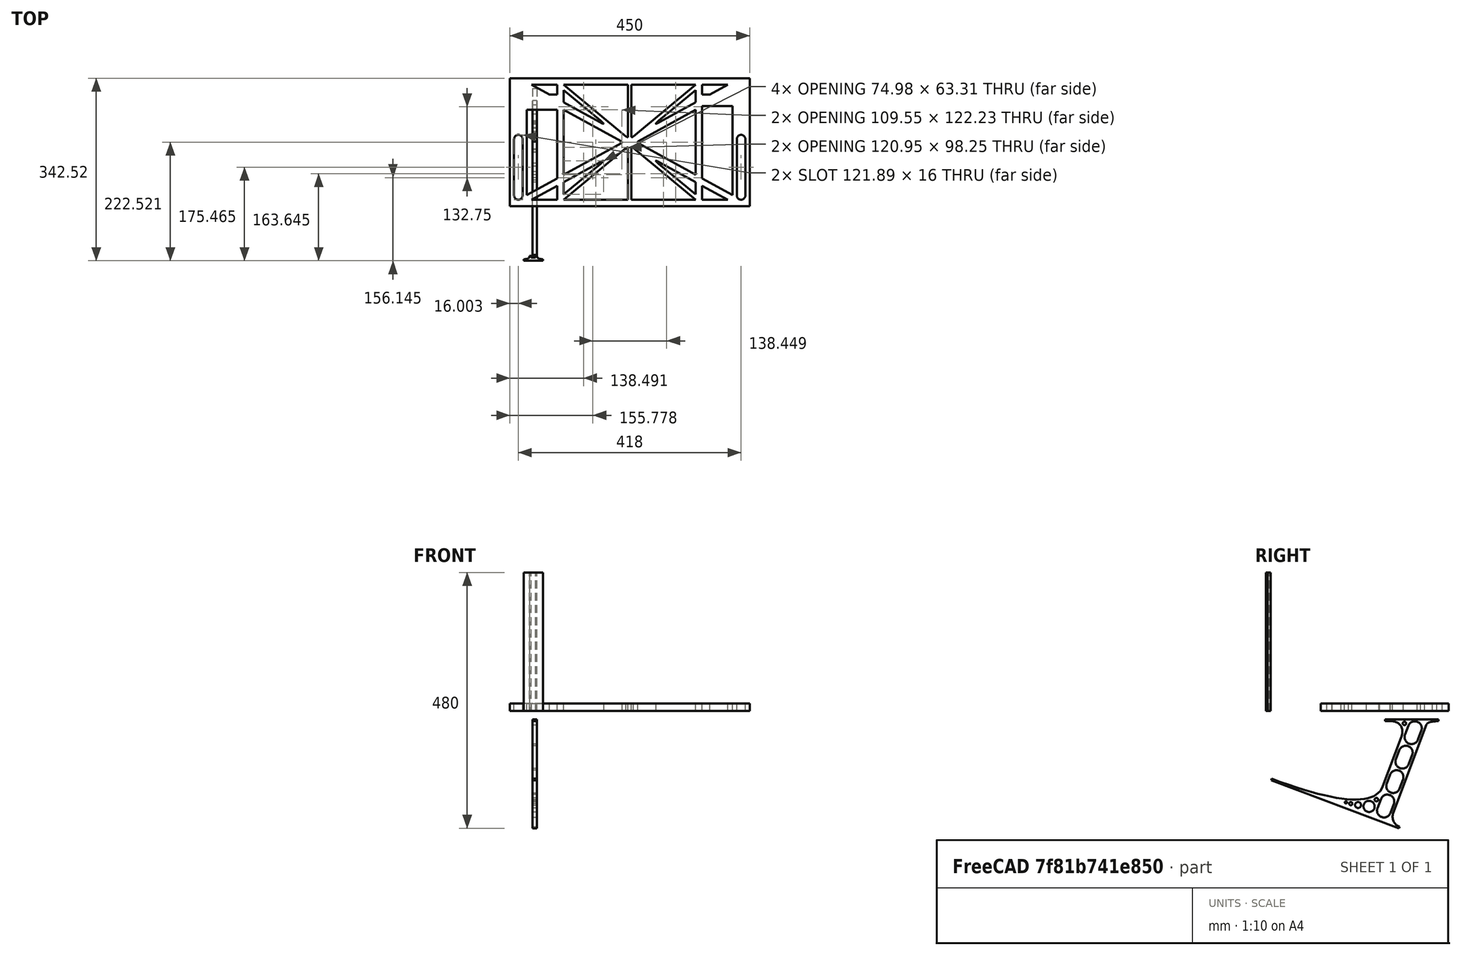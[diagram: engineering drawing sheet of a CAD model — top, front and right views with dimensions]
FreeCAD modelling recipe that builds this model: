
FCSTD DOCUMENT  (FreeCAD 0.19R0.19.2)
Label: laptopStand069
License: All rights reserved
LicenseURL: http://en.wikipedia.org/wiki/All_rights_reserved
objects: Sketcher::SketchObject×3, Part::Extrusion×3
note: 6 computed .brp shape members not serialized (recipe doc carries the construction recipe); baked Part::Feature solids carry a one-line shape summary decoded from their .brp

FEATURE [Sketcher::SketchObject] Sketch
  FullyConstrained = true
  sketch-geometry (124):
    g0: LineSegment StartX=-10.9272 StartY=-82.7794 StartZ=0 EndX=46.0728 EndY=-51.4823 EndZ=0
    g1: LineSegment StartX=366.073 StartY=-91.7794 StartZ=0 EndX=318.073 EndY=-65.424 EndZ=0
    g2: LineSegment StartX=-10.9272 StartY=77.3346 StartZ=0 EndX=-10.9272 EndY=-82.7794 EndZ=0
    g3: LineSegment StartX=375.073 StartY=-82.7794 StartZ=0 EndX=375.073 EndY=83.9235 EndZ=0
    g4: LineSegment StartX=-1.92719 StartY=-91.7794 StartZ=0 EndX=46.0728 EndY=-91.7794 EndZ=0
    g5: LineSegment StartX=318.073 StartY=124.221 StartZ=0 EndX=366.073 EndY=124.221 EndZ=0
    g6: LineSegment StartX=306.073 StartY=124.221 StartZ=0 EndX=189.124 EndY=27.0628 EndZ=0
    g7: LineSegment StartX=58.0728 StartY=-91.7794 StartZ=0 EndX=175.022 EndY=5.37834 EndZ=0
    g8: LineSegment StartX=58.0728 StartY=-81.8102 StartZ=0 EndX=58.0728 EndY=-58.8351 EndZ=0
    g9: LineSegment StartX=306.073 StartY=114.251 StartZ=0 EndX=306.073 EndY=91.2763 EndZ=0
    g10: LineSegment StartX=175.022 StartY=27.0628 StartZ=0 EndX=58.0728 EndY=124.221 EndZ=0
    g11: LineSegment StartX=189.124 StartY=5.37834 StartZ=0 EndX=306.073 EndY=-91.7794 EndZ=0
    g12: LineSegment StartX=306.073 StartY=77.3346 StartZ=0 EndX=306.073 EndY=-44.8935 EndZ=0
    g13: LineSegment StartX=318.073 StartY=83.9235 StartZ=0 EndX=318.073 EndY=-51.4823 EndZ=0
    g14: LineSegment StartX=306.073 StartY=-58.8351 StartZ=0 EndX=306.073 EndY=-81.8102 EndZ=0
    g15: LineSegment StartX=318.073 StartY=-51.4823 StartZ=0 EndX=375.073 EndY=-82.7794 EndZ=0
    g16: LineSegment StartX=318.073 StartY=-65.424 StartZ=0 EndX=318.073 EndY=-91.7794 EndZ=0
    g17: LineSegment StartX=318.073 StartY=-91.7794 StartZ=0 EndX=366.073 EndY=-91.7794 EndZ=0
    g18: LineSegment StartX=58.0728 StartY=-44.8935 StartZ=0 EndX=58.0728 EndY=77.3346 EndZ=0
    g19: LineSegment StartX=46.0728 StartY=-65.424 StartZ=0 EndX=-1.92719 EndY=-91.7794 EndZ=0
    g20: LineSegment StartX=46.0728 StartY=-65.424 StartZ=0 EndX=46.0728 EndY=-91.7794 EndZ=0
    g21: LineSegment StartX=58.0728 StartY=91.2763 StartZ=0 EndX=58.0728 EndY=114.251 EndZ=0
    g22: LineSegment StartX=46.0728 StartY=77.3346 StartZ=0 EndX=46.0728 EndY=-51.4823 EndZ=0
    g23: LineSegment StartX=-42.9272 StartY=136.221 StartZ=0 EndX=-42.9272 EndY=-103.779 EndZ=0
    g24: LineSegment StartX=407.073 StartY=136.221 StartZ=0 EndX=407.073 EndY=-103.779 EndZ=0
    g25: LineSegment StartX=179.022 StartY=27.0628 StartZ=0 EndX=179.022 EndY=124.221 EndZ=0
    g26: LineSegment StartX=185.124 StartY=27.0628 StartZ=0 EndX=185.124 EndY=124.221 EndZ=0
    g27: ArcOfCircle CenterX=-26.9272 CenterY=22.1087 CenterZ=0 NormalX=0 NormalY=0 NormalZ=1 AngleXU=0 Radius=8 StartAngle=1e-16 EndAngle=3.14159
    g28: ArcOfCircle CenterX=-26.9272 CenterY=-83.7794 CenterZ=0 NormalX=0 NormalY=0 NormalZ=1 AngleXU=0 Radius=8 StartAngle=3.14159 EndAngle=6.28319
    g29: LineSegment StartX=-34.9272 StartY=22.1087 StartZ=0 EndX=-34.9272 EndY=-83.7794 EndZ=0
    g30: LineSegment StartX=-18.9272 StartY=22.1087 StartZ=0 EndX=-18.9272 EndY=-83.7794 EndZ=0
    g31: LineSegment StartX=185.124 StartY=-91.7794 StartZ=0 EndX=306.073 EndY=-91.7794 EndZ=0
    g32: LineSegment StartX=179.022 StartY=-91.7794 StartZ=0 EndX=58.0728 EndY=-91.7794 EndZ=0
    g33: LineSegment StartX=306.073 StartY=124.221 StartZ=0 EndX=185.124 EndY=124.221 EndZ=0
    g34: LineSegment StartX=179.022 StartY=124.221 StartZ=0 EndX=58.0728 EndY=124.221 EndZ=0
    g35: ArcOfCircle CenterX=391.073 CenterY=22.1087 CenterZ=0 NormalX=0 NormalY=0 NormalZ=1 AngleXU=0 Radius=8 StartAngle=-4.4e-15 EndAngle=3.14159
    g36: LineSegment StartX=399.073 StartY=22.1087 StartZ=0 EndX=399.073 EndY=-83.7794 EndZ=0
    g37: LineSegment StartX=383.073 StartY=22.1087 StartZ=0 EndX=383.073 EndY=-83.7794 EndZ=0
    g38: ArcOfCircle CenterX=391.073 CenterY=-83.7794 CenterZ=0 NormalX=0 NormalY=0 NormalZ=1 AngleXU=0 Radius=8 StartAngle=3.14159 EndAngle=6.28319
    g39: Circle CenterX=175.022 CenterY=27.0628 CenterZ=0 NormalX=0 NormalY=0 NormalZ=1 AngleXU=0 Radius=1
    g40: Circle CenterX=179.022 CenterY=24.8665 CenterZ=0 NormalX=0 NormalY=0 NormalZ=1 AngleXU=0 Radius=1
    g41: Circle CenterX=179.022 CenterY=27.0628 CenterZ=0 NormalX=0 NormalY=0 NormalZ=1 AngleXU=0 Radius=1
    g42: BSplineCurve PolesCount=3 KnotsCount=2 Degree=2 IsPeriodic=0
    g43: GeomPoint X=175.022 Y=27.0628 Z=0
    g44: GeomPoint X=179.022 Y=27.0628 Z=0
    g45: Circle CenterX=189.124 CenterY=27.0628 CenterZ=0 NormalX=0 NormalY=0 NormalZ=1 AngleXU=0 Radius=1
    g46: Circle CenterX=185.124 CenterY=24.8665 CenterZ=0 NormalX=0 NormalY=0 NormalZ=1 AngleXU=0 Radius=1
    g47: Circle CenterX=185.124 CenterY=27.0628 CenterZ=0 NormalX=0 NormalY=0 NormalZ=1 AngleXU=0 Radius=1
    g48: BSplineCurve PolesCount=3 KnotsCount=2 Degree=2 IsPeriodic=0
    g49: GeomPoint X=189.124 Y=27.0628 Z=0
    g50: GeomPoint X=185.124 Y=27.0628 Z=0
    g51: Circle CenterX=175.022 CenterY=5.37834 CenterZ=0 NormalX=0 NormalY=0 NormalZ=1 AngleXU=0 Radius=1
    g52: Circle CenterX=179.022 CenterY=7.57463 CenterZ=0 NormalX=0 NormalY=0 NormalZ=1 AngleXU=0 Radius=1
    g53: Circle CenterX=179.022 CenterY=5.34704 CenterZ=0 NormalX=0 NormalY=0 NormalZ=1 AngleXU=0 Radius=1
    g54: BSplineCurve PolesCount=3 KnotsCount=2 Degree=2 IsPeriodic=0
    g55: GeomPoint X=175.022 Y=5.37834 Z=0
    g56: GeomPoint X=179.022 Y=5.34704 Z=0
    g57: Circle CenterX=189.124 CenterY=5.37834 CenterZ=0 NormalX=0 NormalY=0 NormalZ=1 AngleXU=0 Radius=1
    g58: Circle CenterX=185.124 CenterY=7.57463 CenterZ=0 NormalX=0 NormalY=0 NormalZ=1 AngleXU=0 Radius=1
    g59: Circle CenterX=185.124 CenterY=5.34704 CenterZ=0 NormalX=0 NormalY=0 NormalZ=1 AngleXU=0 Radius=1
    g60: BSplineCurve PolesCount=3 KnotsCount=2 Degree=2 IsPeriodic=0
    g61: GeomPoint X=189.124 Y=5.37834 Z=0
    g62: GeomPoint X=185.124 Y=5.34704 Z=0
    g63: LineSegment StartX=179.022 StartY=5.34704 StartZ=0 EndX=179.022 EndY=-91.7794 EndZ=0
    g64: LineSegment StartX=185.124 StartY=-91.7794 StartZ=0 EndX=185.124 EndY=5.34704 EndZ=0
    g65: Circle CenterX=165.871 CenterY=18.1458 CenterZ=0 NormalX=0 NormalY=0 NormalZ=1 AngleXU=0 Radius=1
    g66: Circle CenterX=169.377 CenterY=16.2206 CenterZ=0 NormalX=0 NormalY=0 NormalZ=1 AngleXU=0 Radius=1
    g67: Circle CenterX=165.871 CenterY=14.2954 CenterZ=0 NormalX=0 NormalY=0 NormalZ=1 AngleXU=0 Radius=1
    g68: BSplineCurve PolesCount=3 KnotsCount=2 Degree=2 IsPeriodic=0
    g69: GeomPoint X=165.871 Y=18.1458 Z=0
    g70: GeomPoint X=165.871 Y=14.2954 Z=0
    g71: Circle CenterX=198.275 CenterY=18.1458 CenterZ=0 NormalX=0 NormalY=0 NormalZ=1 AngleXU=0 Radius=1
    g72: Circle CenterX=194.768 CenterY=16.2206 CenterZ=0 NormalX=0 NormalY=0 NormalZ=1 AngleXU=0 Radius=1
    g73: Circle CenterX=198.275 CenterY=14.2954 CenterZ=0 NormalX=0 NormalY=0 NormalZ=1 AngleXU=0 Radius=1
    g74: BSplineCurve PolesCount=3 KnotsCount=2 Degree=2 IsPeriodic=0
    g75: GeomPoint X=198.275 Y=18.1458 Z=0
    g76: GeomPoint X=198.275 Y=14.2954 Z=0
    g77: LineSegment StartX=165.871 StartY=18.1458 StartZ=0 EndX=58.0728 EndY=77.3346 EndZ=0
    g78: LineSegment StartX=58.0728 StartY=-44.8935 StartZ=0 EndX=165.871 EndY=14.2954 EndZ=0
    g79: LineSegment StartX=198.275 StartY=18.1458 StartZ=0 EndX=306.073 EndY=77.3346 EndZ=0
    g80: LineSegment StartX=198.275 StartY=14.2954 StartZ=0 EndX=306.073 EndY=-44.8935 EndZ=0
    g81: LineSegment StartX=407.073 StartY=-103.779 StartZ=0 EndX=-42.9272 EndY=-103.779 EndZ=0
    g82: LineSegment StartX=407.073 StartY=136.221 StartZ=0 EndX=-42.9272 EndY=136.221 EndZ=0
    g83: LineSegment StartX=46.0728 StartY=77.3346 StartZ=0 EndX=-10.9272 EndY=77.3346 EndZ=0
    g84: LineSegment StartX=46.0728 StartY=105.865 StartZ=0 EndX=31.5028 EndY=105.865 EndZ=0
    g85: LineSegment StartX=46.0728 StartY=124.221 StartZ=0 EndX=46.0728 EndY=105.865 EndZ=0
    g86: LineSegment StartX=-1.92719 StartY=124.221 StartZ=0 EndX=31.5028 EndY=105.865 EndZ=0
    g87: LineSegment StartX=46.0728 StartY=124.221 StartZ=0 EndX=-1.92719 EndY=124.221 EndZ=0
    g88: LineSegment StartX=318.073 StartY=83.9235 StartZ=0 EndX=375.073 EndY=83.9235 EndZ=0
    g89: LineSegment StartX=318.073 StartY=105.865 StartZ=0 EndX=332.643 EndY=105.865 EndZ=0
    g90: LineSegment StartX=332.643 StartY=105.865 StartZ=0 EndX=366.073 EndY=124.221 EndZ=0
    g91: LineSegment StartX=318.073 StartY=124.221 StartZ=0 EndX=318.073 EndY=105.865 EndZ=0
    g92: Circle CenterX=125.607 CenterY=54.1951 CenterZ=0 NormalX=0 NormalY=0 NormalZ=1 AngleXU=0 Radius=1
    g93: Circle CenterX=139.632 CenterY=46.4944 CenterZ=0 NormalX=0 NormalY=0 NormalZ=1 AngleXU=0 Radius=1
    g94: Circle CenterX=127.325 CenterY=56.7187 CenterZ=0 NormalX=0 NormalY=0 NormalZ=1 AngleXU=0 Radius=1
    g95: BSplineCurve PolesCount=3 KnotsCount=2 Degree=2 IsPeriodic=0
    g96: GeomPoint X=125.607 Y=54.1951 Z=0
    g97: GeomPoint X=127.325 Y=56.7187 Z=0
    g98: LineSegment StartX=127.325 StartY=56.7187 StartZ=0 EndX=58.0728 EndY=114.251 EndZ=0
    g99: LineSegment StartX=58.0728 StartY=91.2763 StartZ=0 EndX=125.607 EndY=54.1951 EndZ=0
    g100: Circle CenterX=236.821 CenterY=56.7187 CenterZ=0 NormalX=0 NormalY=0 NormalZ=1 AngleXU=0 Radius=1
    g101: Circle CenterX=224.513 CenterY=46.4944 CenterZ=0 NormalX=0 NormalY=0 NormalZ=1 AngleXU=0 Radius=1
    g102: Circle CenterX=238.538 CenterY=54.1951 CenterZ=0 NormalX=0 NormalY=0 NormalZ=1 AngleXU=0 Radius=1
    g103: BSplineCurve PolesCount=3 KnotsCount=2 Degree=2 IsPeriodic=0
    g104: GeomPoint X=236.821 Y=56.7187 Z=0
    g105: GeomPoint X=238.538 Y=54.1951 Z=0
    g106: LineSegment StartX=236.821 StartY=56.7187 StartZ=0 EndX=306.073 EndY=114.251 EndZ=0
    g107: LineSegment StartX=238.538 StartY=54.1951 StartZ=0 EndX=306.073 EndY=91.2763 EndZ=0
    g108: Circle CenterX=238.538 CenterY=-21.7539 CenterZ=0 NormalX=0 NormalY=0 NormalZ=1 AngleXU=0 Radius=1
    g109: Circle CenterX=224.513 CenterY=-14.0532 CenterZ=0 NormalX=0 NormalY=0 NormalZ=1 AngleXU=0 Radius=1
    g110: Circle CenterX=236.821 CenterY=-24.2775 CenterZ=0 NormalX=0 NormalY=0 NormalZ=1 AngleXU=0 Radius=1
    g111: BSplineCurve PolesCount=3 KnotsCount=2 Degree=2 IsPeriodic=0
    g112: GeomPoint X=238.538 Y=-21.7539 Z=0
    g113: GeomPoint X=236.821 Y=-24.2775 Z=0
    g114: LineSegment StartX=238.538 StartY=-21.7539 StartZ=0 EndX=306.073 EndY=-58.8351 EndZ=0
    g115: LineSegment StartX=236.821 StartY=-24.2775 StartZ=0 EndX=306.073 EndY=-81.8102 EndZ=0
    g116: Circle CenterX=125.607 CenterY=-21.7539 CenterZ=0 NormalX=0 NormalY=0 NormalZ=1 AngleXU=0 Radius=1
    g117: Circle CenterX=139.632 CenterY=-14.0532 CenterZ=0 NormalX=0 NormalY=0 NormalZ=1 AngleXU=0 Radius=1
    g118: Circle CenterX=127.325 CenterY=-24.2775 CenterZ=0 NormalX=0 NormalY=0 NormalZ=1 AngleXU=0 Radius=1
    g119: BSplineCurve PolesCount=3 KnotsCount=2 Degree=2 IsPeriodic=0
    g120: GeomPoint X=125.607 Y=-21.7539 Z=0
    g121: GeomPoint X=127.325 Y=-24.2775 Z=0
    g122: LineSegment StartX=125.607 StartY=-21.7539 StartZ=0 EndX=58.0728 EndY=-58.8351 EndZ=0
    g123: LineSegment StartX=127.325 StartY=-24.2775 StartZ=0 EndX=58.0728 EndY=-81.8102 EndZ=0
  constraints (224):
    c: Horizontal(g4)
    c: Horizontal(g5)
    c: Tangent(g9,g12)
    c: Tangent(g12,g14)
    c: Coincident(g13,g15)
    c: Coincident(g16,g1)
    c: Tangent(g13,g16)
    c: Tangent(g8,g18)
    c: Coincident(g20,g19)
    c: Coincident(g0,g22)
    c: Tangent(g18,g21)
    c: Block(g10)
    c: Block(g6)
    c: Block(g15)
    c: Block(g3)
    c: Block(g14)
    c: Block(g1)
    c: Block(g16)
    c: Block(g11)
    c: Block(g7)
    c: Block(g20)
    c: Block(g19)
    c: Block(g0)
    c: Block(g2)
    c: Block(g21)
    c: Block(g12)
    c: Block(g5)
    c: Block(g17)
    c: Block(g4)
    c: Vertical(g23)
    c: Vertical(g24)
    c: Block(g24)
    c: Block(g23)
    c: Vertical(g25)
    c: Vertical(g26)
    c: Block(g25)
    c: Block(g26)
    c: Tangent(g27,g30) = 1.5708
    c: Tangent(g27,g29) = -1.5708
    c: Tangent(g29,g28) = -1.5708
    c: Tangent(g30,g28) = 1.5708
    c: Vertical(g29)
    c: Equal(g27,g28)
    c: Block(g30)
    c: Block(g29)
    c: Coincident(g31,g11)
    c: Horizontal(g31)
    c: Coincident(g32,g7)
    c: Horizontal(g32)
    c: Coincident(g33,g6)
    c: Coincident(g33,g26)
    c: Horizontal(g33)
    c: Coincident(g34,g25)
    c: Coincident(g34,g10)
    c: Horizontal(g34)
    c: Tangent(g35,g36) = 1.5708
    c: Tangent(g36,g38) = 1.5708
    c: Equal(g35,g38)
    c: Coincident(g37,g35)
    c: Coincident(g37,g38)
    c: Block(g36)
    c: Block(g37)
    c: Coincident(g42,g10)
    c: Weight(g39) = 1
    c: Equal(g39,g40)
    c: Equal(g39,g41)
    c: Coincident(g42,g25)
    c: InternalAlignment(g39,g42)
    c: InternalAlignment(g40,g42)
    c: InternalAlignment(g41,g42)
    c: InternalAlignment(g43,g42)
    c: InternalAlignment(g44,g42)
    c: Coincident(g48,g6)
    c: Weight(g45) = 1
    c: Equal(g45,g46)
    c: Equal(g45,g47)
    c: Coincident(g48,g26)
    c: InternalAlignment(g45,g48)
    c: InternalAlignment(g46,g48)
    c: InternalAlignment(g47,g48)
    c: InternalAlignment(g49,g48)
    c: InternalAlignment(g50,g48)
    c: Block(g48)
    c: Block(g42)
    c: Coincident(g54,g7)
    c: Weight(g51) = 1
    c: Equal(g51,g52)
    c: Equal(g51,g53)
    c: InternalAlignment(g51,g54)
    c: InternalAlignment(g52,g54)
    c: InternalAlignment(g53,g54)
    c: InternalAlignment(g55,g54)
    c: InternalAlignment(g56,g54)
    c: Weight(g57) = 1
    c: Equal(g57,g58)
    c: Equal(g57,g59)
    c: InternalAlignment(g57,g60)
    c: InternalAlignment(g58,g60)
    c: InternalAlignment(g59,g60)
    c: InternalAlignment(g61,g60)
    c: InternalAlignment(g62,g60)
    c: Block(g60)
    c: Block(g54)
    c: Coincident(g63,g54)
    c: Coincident(g63,g32)
    c: Vertical(g63)
    c: Coincident(g64,g31)
    c: Coincident(g64,g60)
    c: Vertical(g64)
    c: Weight(g65) = 1
    c: Equal(g65,g66)
    c: Equal(g65,g67)
    c: InternalAlignment(g65,g68)
    c: InternalAlignment(g66,g68)
    c: InternalAlignment(g67,g68)
    c: InternalAlignment(g69,g68)
    c: InternalAlignment(g70,g68)
    c: Weight(g71) = 1
    c: Equal(g71,g72)
    c: Equal(g71,g73)
    c: InternalAlignment(g71,g74)
    c: InternalAlignment(g72,g74)
    c: InternalAlignment(g73,g74)
    c: InternalAlignment(g75,g74)
    c: InternalAlignment(g76,g74)
    c: Block(g68)
    c: Block(g74)
    c: Coincident(g77,g68)
    c: Coincident(g77,g18)
    c: Coincident(g78,g18)
    c: Coincident(g78,g68)
    c: Coincident(g79,g74)
    c: Coincident(g79,g12)
    c: Coincident(g80,g74)
    c: Coincident(g80,g12)
    c: Block(g18)
    c: Coincident(g81,g24)
    c: Coincident(g81,g23)
    c: Horizontal(g81)
    c: Distance(g81) = 450
    c: Coincident(g82,g24)
    c: Coincident(g82,g23)
    c: Horizontal(g82)
    c: Horizontal(g83)
    c: Coincident(g22,g83)
    c: Horizontal(g84)
    c: Vertical(g85)
    c: Block(g85)
    c: Block(g84)
    c: Block(g83)
    c: Distance(g85) = 18.3554
    c: Coincident(g87,g85)
    c: Coincident(g87,g86)
    c: Horizontal(g87)
    c: Block(g87)
    c: Block(g86)
    c: Coincident(g84,g86)
    c: Coincident(g2,g83)
    c: Coincident(g88,g13)
    c: Horizontal(g88)
    c: Horizontal(g89)
    c: Block(g88)
    c: Block(g9)
    c: Coincident(g90,g5)
    c: Coincident(g91,g5)
    c: Coincident(g91,g89)
    c: Vertical(g91)
    c: Block(g91)
    c: Coincident(g89,g90)
    c: Block(g90)
    c: Coincident(g3,g88)
    c: Weight(g92) = 1
    c: Equal(g92,g93)
    c: Equal(g92,g94)
    c: InternalAlignment(g92,g95)
    c: InternalAlignment(g93,g95)
    c: InternalAlignment(g94,g95)
    c: InternalAlignment(g96,g95)
    c: InternalAlignment(g97,g95)
    c: Block(g95)
    c: Coincident(g98,g95)
    c: Coincident(g98,g21)
    c: Coincident(g99,g21)
    c: Coincident(g99,g95)
    c: Weight(g100) = 1
    c: Equal(g100,g101)
    c: Equal(g100,g102)
    c: InternalAlignment(g100,g103)
    c: InternalAlignment(g101,g103)
    c: InternalAlignment(g102,g103)
    c: InternalAlignment(g104,g103)
    c: InternalAlignment(g105,g103)
    c: Block(g103)
    c: Coincident(g106,g103)
    c: Coincident(g106,g9)
    c: Coincident(g107,g103)
    c: Coincident(g107,g9)
    c: Weight(g108) = 1
    c: Equal(g108,g109)
    c: Equal(g108,g110)
    c: InternalAlignment(g108,g111)
    c: InternalAlignment(g109,g111)
    c: InternalAlignment(g110,g111)
    c: InternalAlignment(g112,g111)
    c: InternalAlignment(g113,g111)
    c: Block(g111)
    c: Coincident(g114,g111)
    c: Coincident(g114,g14)
    c: Coincident(g115,g111)
    c: Coincident(g115,g14)
    c: Weight(g116) = 1
    c: Equal(g116,g117)
    c: Equal(g116,g118)
    c: InternalAlignment(g116,g119)
    c: InternalAlignment(g117,g119)
    c: InternalAlignment(g118,g119)
    c: InternalAlignment(g120,g119)
    c: InternalAlignment(g121,g119)
    c: Block(g119)
    c: Coincident(g122,g119)
    c: Coincident(g122,g8)
    c: Coincident(g123,g119)
    c: Coincident(g123,g8)
    c: Block(g8)
FEATURE [Sketcher::SketchObject] Sketch001
  FullyConstrained = true
  MapMode = 4
  Placement = pos=(0,0,0) rot=(0.57735,0.57735,0.57735;2.0944rad)
  Support = -> [Sketch]
  sketch-geometry (46):
    g0: BSplineCurve PolesCount=3 KnotsCount=2 Degree=2 IsPeriodic=0
    g1: ArcOfCircle CenterX=73.1223 CenterY=-32.291 CenterZ=0 NormalX=0 NormalY=0 NormalZ=1 AngleXU=0 Radius=13 StartAngle=5.92268 EndAngle=9.06428
    g2: ArcOfCircle CenterX=66.7816 CenterY=-49.1439 CenterZ=0 NormalX=0 NormalY=0 NormalZ=1 AngleXU=0 Radius=13 StartAngle=2.78068 EndAngle=5.92131
    g3: ArcOfCircle CenterX=55.9263 CenterY=-78.1807 CenterZ=0 NormalX=0 NormalY=0 NormalZ=1 AngleXU=0 Radius=13 StartAngle=5.92268 EndAngle=9.06428
    g4: ArcOfCircle CenterX=49.5884 CenterY=-95.0342 CenterZ=0 NormalX=0 NormalY=0 NormalZ=1 AngleXU=0 Radius=13 StartAngle=2.78068 EndAngle=5.92131
    g5: ArcOfCircle CenterX=38.7206 CenterY=-124.067 CenterZ=0 NormalX=0 NormalY=0 NormalZ=1 AngleXU=0 Radius=13 StartAngle=5.92268 EndAngle=9.06428
    g6: ArcOfCircle CenterX=32.3875 CenterY=-140.92 CenterZ=0 NormalX=0 NormalY=0 NormalZ=1 AngleXU=0 Radius=13 StartAngle=2.78068 EndAngle=5.92131
    g7: ArcOfCircle CenterX=21.4715 CenterY=-169.934 CenterZ=0 NormalX=0 NormalY=0 NormalZ=1 AngleXU=0 Radius=13 StartAngle=5.92268 EndAngle=9.06428
    g8: ArcOfCircle CenterX=15.1336 CenterY=-186.787 CenterZ=0 NormalX=0 NormalY=0 NormalZ=1 AngleXU=0 Radius=13 StartAngle=2.78068 EndAngle=5.92131
    g9-g12: Circle x4 (B-spline internal-alignment scaffolding for g13; pole/knot coordinates omitted)
    g13: BSplineCurve PolesCount=4 KnotsCount=2 Degree=3 IsPeriodic=0
    g14: GeomPoint X=28.8094 Y=-19.0875 Z=0
    g15: GeomPoint X=47.0443 Y=-50.4712 Z=0
    g16: Circle CenterX=53.5586 CenterY=-23.2695 CenterZ=0 NormalX=0 NormalY=0 NormalZ=1 AngleXU=0 Radius=3.24518
    g17: Circle CenterX=-195.441 CenterY=-127.082 CenterZ=0 NormalX=0 NormalY=0 NormalZ=1 AngleXU=0 Radius=1
    g18: Circle CenterX=-8.24091 CenterY=-197.481 CenterZ=0 NormalX=0 NormalY=0 NormalZ=1 AngleXU=0 Radius=1
    g19: Circle CenterX=12.8789 CenterY=-141.321 CenterZ=0 NormalX=0 NormalY=0 NormalZ=1 AngleXU=0 Radius=1
    g20: BSplineCurve PolesCount=3 KnotsCount=2 Degree=2 IsPeriodic=0
    g21: GeomPoint X=-195.441 Y=-127.082 Z=0
    g22: GeomPoint X=12.8789 Y=-141.321 Z=0
    g23: Circle CenterX=-12.8016 CenterY=-179.036 CenterZ=0 NormalX=0 NormalY=0 NormalZ=1 AngleXU=0 Radius=10.5072
    g24: Circle CenterX=0.933922 CenterY=-166.43 CenterZ=0 NormalX=0 NormalY=0 NormalZ=1 AngleXU=0 Radius=3.26661
    g25: Circle CenterX=-33.5518 CenterY=-176.44 CenterZ=0 NormalX=0 NormalY=0 NormalZ=1 AngleXU=0 Radius=5.64388
    g26: Circle CenterX=-47.2366 CenterY=-173.859 CenterZ=0 NormalX=0 NormalY=0 NormalZ=1 AngleXU=0 Radius=3.01653
    g27: Circle CenterX=-56.2595 CenterY=-171.456 CenterZ=0 NormalX=0 NormalY=0 NormalZ=1 AngleXU=0 Radius=2.12826
    g28: ArcOfCircle CenterX=51.2151 CenterY=-198.473 CenterZ=0 NormalX=0 NormalY=0 NormalZ=1 AngleXU=0 Radius=20 StartAngle=2.78189 EndAngle=4.35269
    g29: LineSegment StartX=32.4951 StartY=-191.433 StartZ=0 EndX=94.6578 EndY=-26.1352 EndZ=0
    g30: LineSegment StartX=43.1192 StartY=-220.001 StartZ=0 EndX=-196.497 EndY=-129.89 EndZ=0
    g31: LineSegment StartX=43.1192 StartY=-220.001 StartZ=0 EndX=44.1752 EndY=-217.193 EndZ=0
    g32: LineSegment StartX=117.223 StartY=-19.0875 StartZ=0 EndX=117.223 EndY=-16.0875 EndZ=0
    g33: LineSegment StartX=117.223 StartY=-16.0875 StartZ=0 EndX=17.2232 EndY=-16.0875 EndZ=0
    g34: LineSegment StartX=17.2232 StartY=-16.0875 StartZ=0 EndX=17.2232 EndY=-19.0875 EndZ=0
    g35: LineSegment StartX=28.8094 StartY=-19.0875 StartZ=0 EndX=17.2232 EndY=-19.0875 EndZ=0
    g36: LineSegment StartX=47.0443 StartY=-50.4712 StartZ=0 EndX=12.8789 EndY=-141.321 EndZ=0
    g37: LineSegment StartX=-195.441 StartY=-127.082 StartZ=0 EndX=-196.497 EndY=-129.89 EndZ=0
    g38: LineSegment StartX=85.2866 StartY=-36.8766 StartZ=0 EndX=78.9396 EndY=-53.7463 EndZ=0
    g39: LineSegment StartX=60.9579 StartY=-27.7053 StartZ=0 EndX=54.6191 EndY=-44.5532 EndZ=0
    g40: LineSegment StartX=68.0907 StartY=-82.7664 StartZ=0 EndX=61.7465 EndY=-99.6365 EndZ=0
    g41: LineSegment StartX=43.7619 StartY=-73.595 StartZ=0 EndX=37.426 EndY=-90.4435 EndZ=0
    g42: LineSegment StartX=50.885 StartY=-128.652 StartZ=0 EndX=44.5456 EndY=-145.522 EndZ=0
    g43: LineSegment StartX=26.5562 StartY=-119.481 StartZ=0 EndX=20.2251 EndY=-136.329 EndZ=0
    g44: LineSegment StartX=9.3071 StartY=-165.349 StartZ=0 EndX=2.97115 EndY=-182.197 EndZ=0
    g45: LineSegment StartX=33.6358 StartY=-174.52 StartZ=0 EndX=27.2917 EndY=-191.39 EndZ=0
  constraints (71):
    c: Block(g0)
    c: Block(g1)
    c: Block(g2)
    c: Block(g4)
    c: Block(g3)
    c: Block(g6)
    c: Block(g5)
    c: Block(g8)
    c: Block(g7)
    c: Weight(g9) = 1
    c: Equal(g9,g10)
    c: Equal(g9,g11)
    c: Equal(g9,g12)
    c: InternalAlignment(g9-g12 -> g13) x4
    c: InternalAlignment(g14,g13)
    c: InternalAlignment(g15,g13)
    c: Block(g16)
    c: Weight(g17) = 1
    c: Equal(g17,g18)
    c: Equal(g17,g19)
    c: InternalAlignment(g17,g20)
    c: InternalAlignment(g18,g20)
    c: InternalAlignment(g19,g20)
    c: InternalAlignment(g21,g20)
    c: InternalAlignment(g22,g20)
    c: Block(g20)
    c: Block(g23)
    c: Block(g24)
    c: Block(g25)
    c: Block(g26)
    c: Block(g27)
    c: Block(g28)
    c: Coincident(g29,g28)
    c: Coincident(g29,g0)
    c: Block(g13)
    c: Coincident(g31,g30)
    c: Coincident(g31,g28)
    c: Block(g31)
    c: Coincident(g32,g0)
    c: Vertical(g32)
    c: Coincident(g33,g32)
    c: Horizontal(g33)
    c: Coincident(g34,g33)
    c: Vertical(g34)
    c: Block(g33)
    c: Coincident(g35,g13)
    c: Coincident(g35,g34)
    c: Horizontal(g35)
    c: Coincident(g36,g13)
    c: Coincident(g36,g20)
    c: Coincident(g37,g20)
    c: Coincident(g37,g30)
    c: Block(g30)
    c: Coincident(g38,g1)
    c: Coincident(g38,g2)
    c: Coincident(g39,g1)
    c: Coincident(g39,g2)
    c: Coincident(g40,g3)
    c: Coincident(g40,g4)
    c: Coincident(g41,g3)
    c: Coincident(g41,g4)
    c: Coincident(g42,g5)
    c: Coincident(g42,g6)
    c: Coincident(g43,g5)
    c: Coincident(g43,g6)
    c: Coincident(g44,g7)
    c: Coincident(g44,g8)
    c: Coincident(g45,g7)
    c: Coincident(g45,g8)
    c: Distance(g30) = 256
    c: Distance(g33) = 100
FEATURE [Part::Extrusion] Extrude002
  Base = -> Sketch001
  Dir = (1,0,0)
  DirMode = 2
  FaceMakerClass = Part::FaceMakerBullseye
  LengthFwd = 8
  LengthRev = 0
  Solid = true
  Symmetric = false
FEATURE [Sketcher::SketchObject] Sketch002
  FullyConstrained = true
  sketch-geometry (20):
    g0: LineSegment StartX=-2.77179 StartY=-200.304 StartZ=0 EndX=5.22821 EndY=-200.304 EndZ=0
    g1: LineSegment StartX=5.22821 StartY=-200.304 StartZ=0 EndX=5.22821 EndY=-197.304 EndZ=0
    g2: LineSegment StartX=-2.77179 StartY=-200.304 StartZ=0 EndX=-2.77179 EndY=-197.304 EndZ=0
    g3: LineSegment StartX=5.22821 StartY=-197.304 StartZ=0 EndX=8.22821 EndY=-197.304 EndZ=0
    g4: LineSegment StartX=-2.77179 StartY=-197.304 StartZ=0 EndX=-5.77179 EndY=-197.304 EndZ=0
    g5: LineSegment StartX=19.2282 StartY=-203.304 StartZ=0 EndX=19.2282 EndY=-206.304 EndZ=0
    g6: LineSegment StartX=-16.7718 StartY=-203.304 StartZ=0 EndX=-16.7718 EndY=-206.304 EndZ=0
    g7: LineSegment StartX=-16.7718 StartY=-206.304 StartZ=0 EndX=19.2282 EndY=-206.304 EndZ=0
    g8: Circle CenterX=-16.7718 CenterY=-203.304 CenterZ=0 NormalX=0 NormalY=0 NormalZ=1 AngleXU=0 Radius=1
    g9: Circle CenterX=-5.77179 CenterY=-203.304 CenterZ=0 NormalX=0 NormalY=0 NormalZ=1 AngleXU=0 Radius=1
    g10: Circle CenterX=-5.77179 CenterY=-197.304 CenterZ=0 NormalX=0 NormalY=0 NormalZ=1 AngleXU=0 Radius=1
    g11: BSplineCurve PolesCount=3 KnotsCount=2 Degree=2 IsPeriodic=0
    g12: GeomPoint X=-16.7718 Y=-203.304 Z=0
    g13: GeomPoint X=-5.77179 Y=-197.304 Z=0
    g14: Circle CenterX=19.2282 CenterY=-203.304 CenterZ=0 NormalX=0 NormalY=0 NormalZ=1 AngleXU=0 Radius=1
    g15: Circle CenterX=8.22821 CenterY=-203.304 CenterZ=0 NormalX=0 NormalY=0 NormalZ=1 AngleXU=0 Radius=1
    g16: Circle CenterX=8.22821 CenterY=-197.304 CenterZ=0 NormalX=0 NormalY=0 NormalZ=1 AngleXU=0 Radius=1
    g17: BSplineCurve PolesCount=3 KnotsCount=2 Degree=2 IsPeriodic=0
    g18: GeomPoint X=19.2282 Y=-203.304 Z=0
    g19: GeomPoint X=8.22821 Y=-197.304 Z=0
  constraints (41):
    c: Horizontal(g0)
    c: Distance(g0) = 8
    c: Coincident(g1,g0)
    c: Vertical(g1)
    c: Distance(g1) = 3
    c: Coincident(g2,g0)
    c: Vertical(g2)
    c: Distance(g2) = 3
    c: Coincident(g3,g1)
    c: Horizontal(g3)
    c: Distance(g3) = 3
    c: Coincident(g4,g2)
    c: Horizontal(g4)
    c: Distance(g4) = 3
    c: Vertical(g5)
    c: Vertical(g6)
    c: Coincident(g7,g6)
    c: Coincident(g7,g5)
    c: Weight(g8) = 1
    c: Equal(g8,g9)
    c: Equal(g8,g10)
    c: Coincident(g11,g4)
    c: InternalAlignment(g8,g11)
    c: InternalAlignment(g9,g11)
    c: InternalAlignment(g10,g11)
    c: InternalAlignment(g12,g11)
    c: InternalAlignment(g13,g11)
    c: Coincident(g17,g5)
    c: Weight(g14) = 1
    c: Equal(g14,g15)
    c: Equal(g14,g16)
    c: Coincident(g17,g3)
    c: InternalAlignment(g14,g17)
    c: InternalAlignment(g15,g17)
    c: InternalAlignment(g16,g17)
    c: InternalAlignment(g18,g17)
    c: InternalAlignment(g19,g17)
    c: Block(g7)
    c: Block(g17)
    c: Block(g11)
    c: Block(g6)
FEATURE [Part::Extrusion] Extrude003
  Base = -> Sketch002
  Dir = (0,0,1)
  DirMode = 2
  FaceMakerClass = Part::FaceMakerBullseye
  LengthFwd = 260
  LengthRev = 0
  Solid = true
  Symmetric = false
FEATURE [Part::Extrusion] Extrude
  Base = -> Sketch
  Dir = (0,0,1)
  DirMode = 2
  FaceMakerClass = Part::FaceMakerBullseye
  LengthFwd = 14
  LengthRev = 0
  Solid = true
  Symmetric = false
